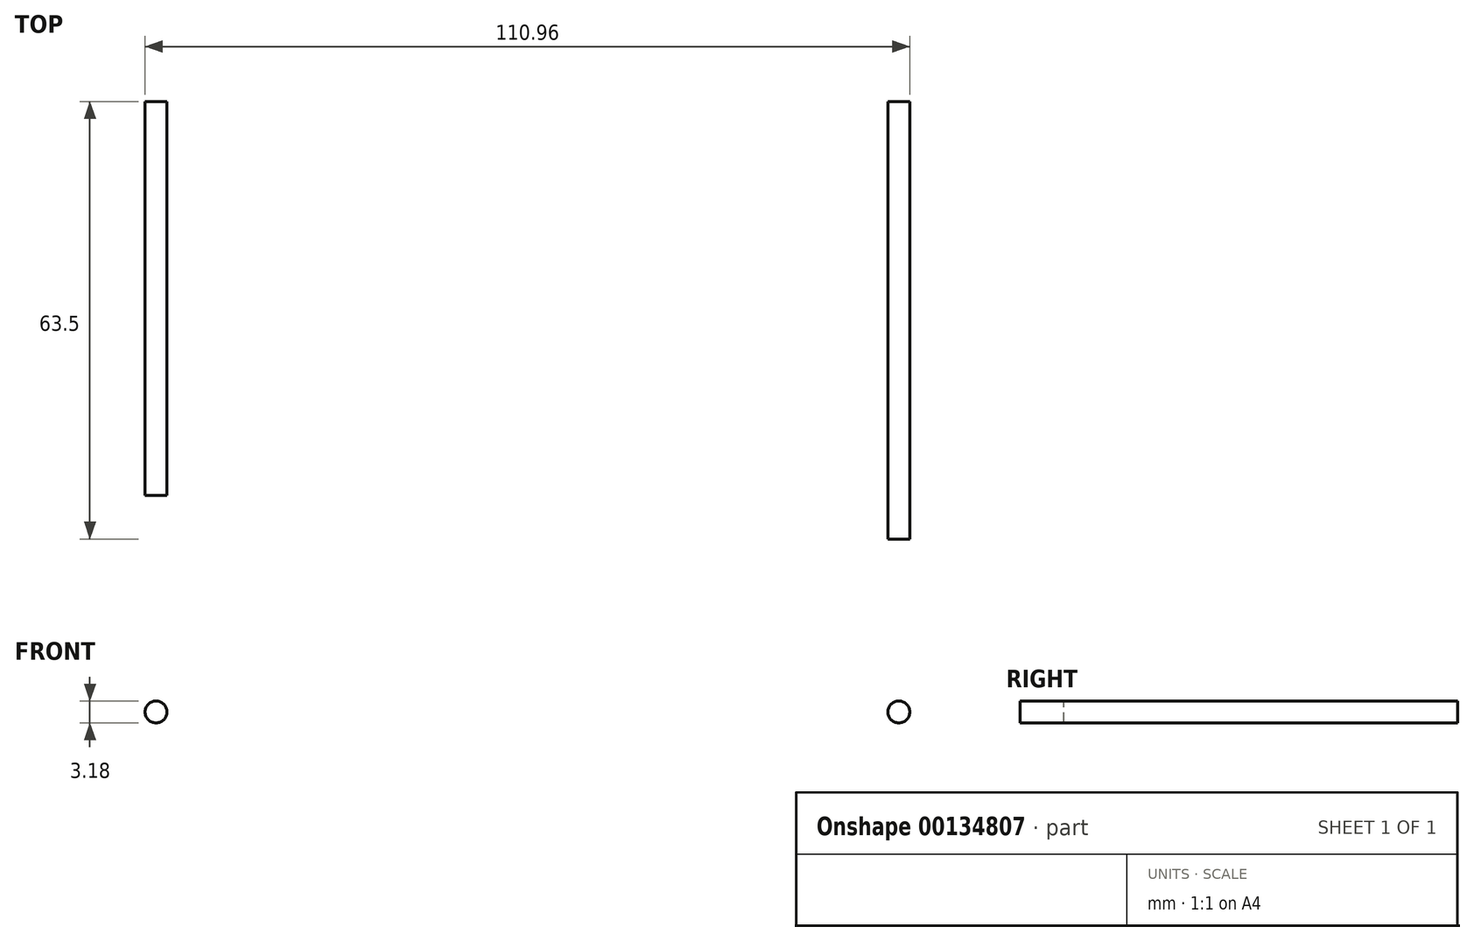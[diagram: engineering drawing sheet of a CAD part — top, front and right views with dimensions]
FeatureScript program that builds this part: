
annotation { "Feature Type Name" : "Feature", "Feature Type Description" : "" }
export const myFeature = defineFeature(function(context is Context, id is Id, definition is map)
    precondition{}
    {
        {
            var Q0;
            Q0=qCreatedBy(makeId("Front.planeOp"),FACE);
            var sketch = newSketch(context, id + "F0", { "sketchPlane" : qUnion([Q0])});
            skCircle(sketch, "E0", {"center": v(-61.98, 0) * mm, "radius": 1.59 * mm});
            skSolve(sketch);
        }
        {
            var Q0;
            Q0=qCreatedBy(makeId("Front.planeOp"),FACE);
            var sketch = newSketch(context, id + "F1", { "sketchPlane" : qUnion([Q0])});
            skCircle(sketch, "E1", {"center": v(45.82, 0) * mm, "radius": 1.59 * mm});
            skSolve(sketch);
        }
        {
            var Q0;
            Q0=makeQuery(id+"F0.imprint","IMPRINT",FACE,{"disambiguationData":[TD([[makeQuery(id+"F0.imprint","IMPRINT",EDGE,{"derivedFrom":sQuery(id+"F0.wireOp",EDGE,"E0")}),1.0]])]});
            extrude(context, id + "F2", {"entities" : qUnion([Q0]), "depth" : 57.15 * mm});
        }
        {
            var Q0;
            Q0 = qSketchRegion(id + "F1", true);
            extrude(context, id + "F3", {"entities" : qUnion([Q0]), "depth" : 63.5 * mm});
        }
    });
